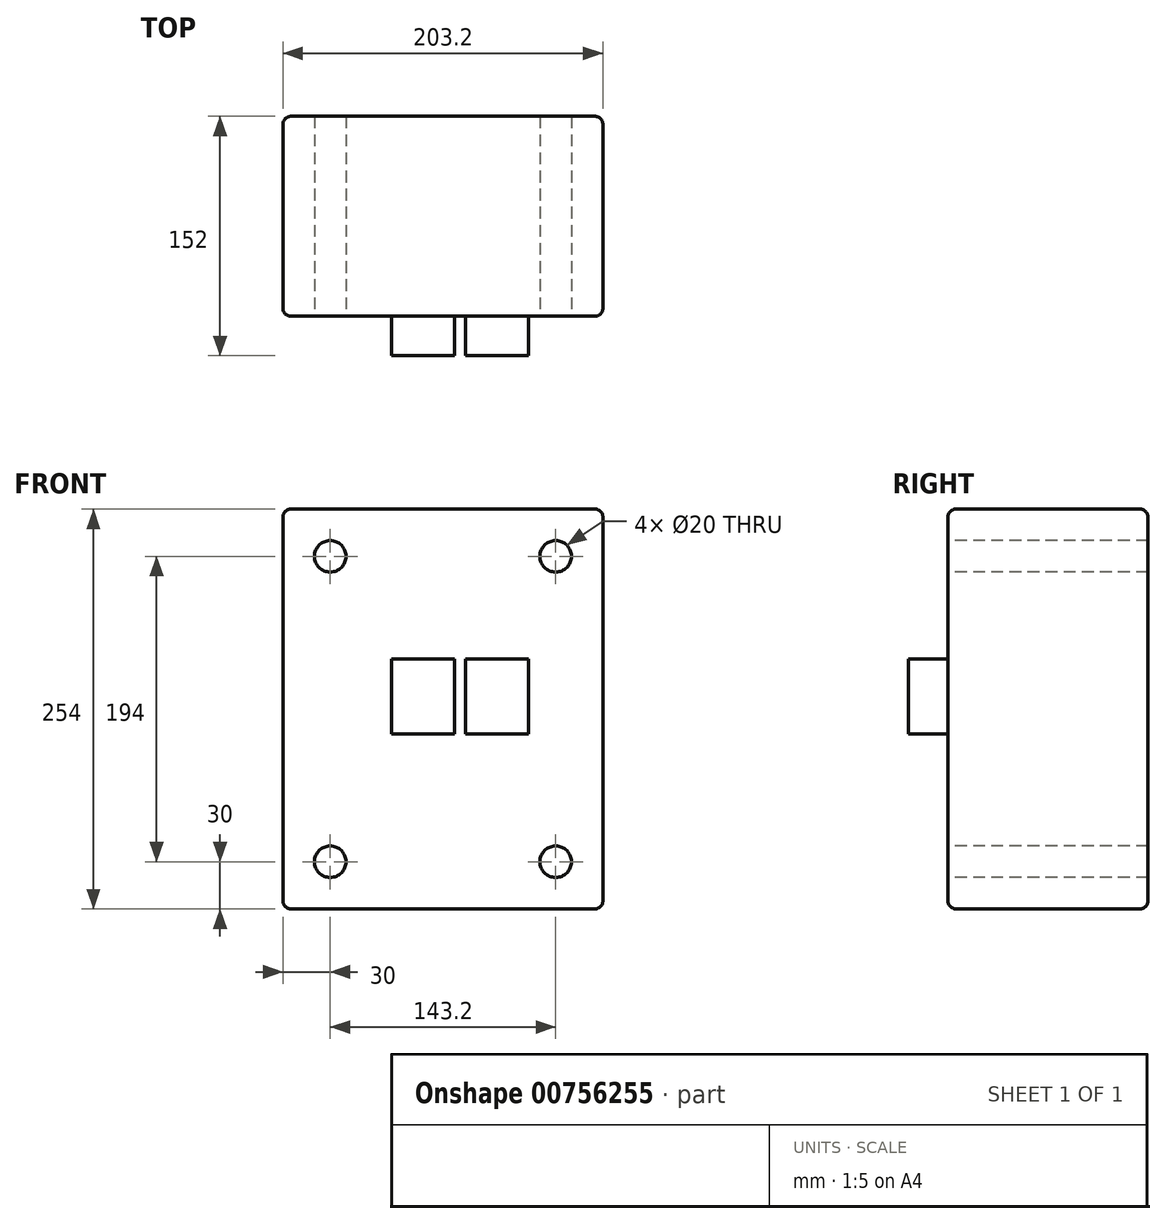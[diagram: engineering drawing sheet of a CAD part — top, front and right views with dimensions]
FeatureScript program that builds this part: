
annotation { "Feature Type Name" : "Feature", "Feature Type Description" : "" }
export const myFeature = defineFeature(function(context is Context, id is Id, definition is map)
    precondition{}
    {
        {
            var Q0;
            Q0=qCreatedBy(makeId("Front.planeOp"),FACE);
            var sketch = newSketch(context, id + "F0", { "sketchPlane" : qUnion([Q0])});
            skLineSegment(sketch, "E0.bottom", {"start": v(101.6, 127) * mm, "end": v(-101.6, 127) * mm});
            skLineSegment(sketch, "E0.top", {"start": v(101.6, -127) * mm, "end": v(-101.6, -127) * mm});
            skLineSegment(sketch, "E0.left", {"start": v(101.6, 127) * mm, "end": v(101.6, -127) * mm});
            skLineSegment(sketch, "E0.right", {"start": v(-101.6, 127) * mm, "end": v(-101.6, -127) * mm});
            skPoint(sketch, "E0.middle", {"position": v(0, 0) * mm});
            skSolve(sketch);
        }
        {
            var Q0;
            Q0 = qSketchRegion(id + "F0", true);
            extrude(context, id + "F1", {"entities" : qUnion([Q0]), "depth" : 127 * mm, "offsetDistance" : 25.4 * mm});
        }
        {
            var Q0;
            Q0=makeQuery(id+"F1.opExtrude","SWEPT_EDGE",EDGE,{"disambiguationData":[OSD([sQuery(id+"F0.wireOp",EDGE,"E0.bottom"),sQuery(id+"F0.wireOp",EDGE,"E0.right")])]});
            var Q1;
            Q1=makeQuery(id+"F1.opExtrude","SWEPT_FACE",FACE,{"disambiguationData":[OSD([sQuery(id+"F0.wireOp",EDGE,"E0.bottom")])]});
            var Q2;
            Q2=makeQuery(id+"F1.opExtrude","SWEPT_FACE",FACE,{"disambiguationData":[OSD([sQuery(id+"F0.wireOp",EDGE,"E0.top")])]});
            var Q3;
            Q3=makeQuery(id+"F1.opExtrude","SWEPT_FACE",FACE,{"disambiguationData":[OSD([sQuery(id+"F0.wireOp",EDGE,"E0.right")])]});
            var Q4;
            Q4=makeQuery(id+"F1.opExtrude","SWEPT_FACE",FACE,{"disambiguationData":[OSD([sQuery(id+"F0.wireOp",EDGE,"E0.left")])]});
            fillet(context, id + "F2", {"entities" : qUnion([Q0, Q1, Q2, Q3, Q4]), "radius" : 5.08 * mm, "tangentPropagation" : true, "allowEdgeOverflow" : false});
        }
        {
            var Q0;
            Q0=makeQuery(id+"F1.opExtrude","CAP_FACE",FACE,{"disambiguationData":[OSD([sQuery(id+"F0.wireOp",EDGE,"E0.bottom"),sQuery(id+"F0.wireOp",EDGE,"E0.top"),sQuery(id+"F0.wireOp",EDGE,"E0.left"),sQuery(id+"F0.wireOp",EDGE,"E0.right")])],"isStart":false});
            var sketch = newSketch(context, id + "F3", { "sketchPlane" : qUnion([Q0])});
            skCircle(sketch, "E1", {"center": v(-71.6, 97) * mm, "radius": 10 * mm});
            skLineSegment(sketch, "E2", {"start": v(0, 121.92) * mm, "end": v(0, -121.92) * mm, "construction": true});
            skCircle(sketch, "E3.MirrorC", {"center": v(71.6, 97) * mm, "radius": 10 * mm});
            skLineSegment(sketch, "E4", {"start": v(-96.52, 0) * mm, "end": v(96.52, 0) * mm, "construction": true});
            skCircle(sketch, "E5.MirrorC", {"center": v(71.6, -97) * mm, "radius": 10 * mm});
            skCircle(sketch, "E6.MirrorC", {"center": v(-71.6, -97) * mm, "radius": 10 * mm});
            skSolve(sketch);
        }
        {
            var Q0;
            Q0 = qSketchRegion(id + "F3", true);
            extrude(context, id + "F4", {"entities" : qUnion([Q0]), "operationType" : NewBodyOperationType.REMOVE, "oppositeDirection" : true, "depth" : 200 * mm, "offsetDistance" : 25 * mm});
        }
        {
            var Q0;
            Q0=makeQuery(id+"F1.opExtrude","CAP_FACE",FACE,{"disambiguationData":[OSD([sQuery(id+"F0.wireOp",EDGE,"E0.bottom"),sQuery(id+"F0.wireOp",EDGE,"E0.top"),sQuery(id+"F0.wireOp",EDGE,"E0.left"),sQuery(id+"F0.wireOp",EDGE,"E0.right")])],"isStart":false});
            var sketch = newSketch(context, id + "F5", { "sketchPlane" : qUnion([Q0])});
            skLineSegment(sketch, "E7", {"start": v(0, 121.92) * mm, "end": v(0, -121.92) * mm, "construction": true});
            skLineSegment(sketch, "E8", {"start": v(-96.52, 0) * mm, "end": v(96.52, 0) * mm, "construction": true});
            skText(sketch, "E9", { "text": "나는", "fontName": "OpenSans-Regular.ttf"});
            const initialGuessF5  = {"E9": [-0.0362, -0.0199, 1, 0, 0.056]};
            skSetInitialGuess(sketch, initialGuessF5);
            skSolve(sketch);
        }
        {
            var Q0;
            Q0 = qSketchRegion(id + "F5", true);
            extrude(context, id + "F6", {"entities" : qUnion([Q0]), "operationType" : NewBodyOperationType.ADD, "depth" : 25 * mm, "offsetDistance" : 25 * mm});
        }
    });
